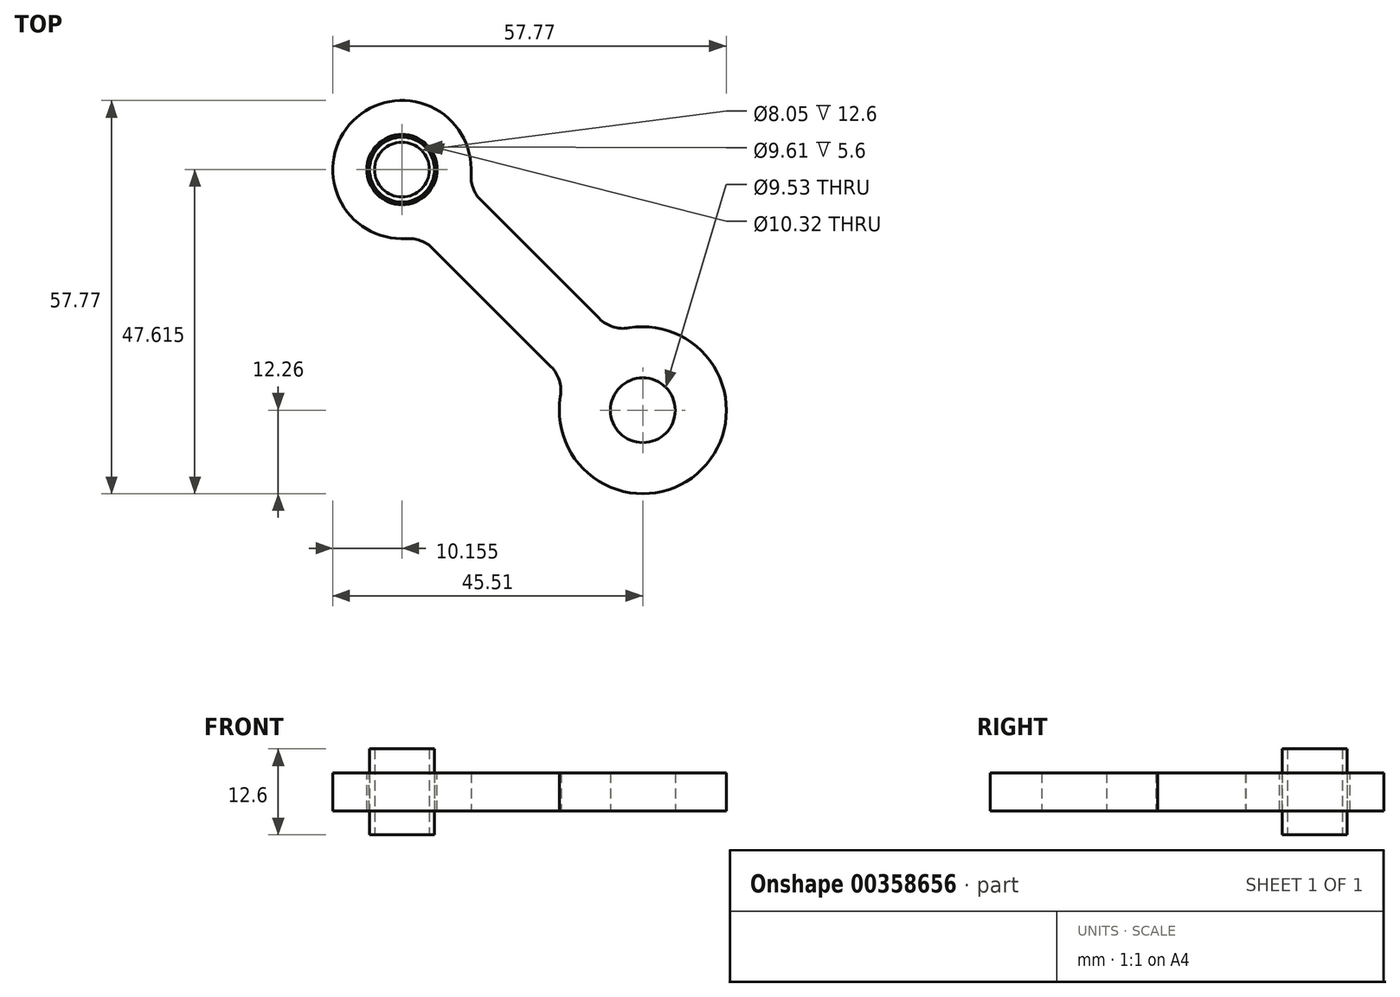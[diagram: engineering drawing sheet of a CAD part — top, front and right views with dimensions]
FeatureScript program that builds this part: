
annotation { "Feature Type Name" : "Feature", "Feature Type Description" : "" }
export const myFeature = defineFeature(function(context is Context, id is Id, definition is map)
    precondition{}
    {
        {
            var Q0;
            Q0=qCreatedBy(makeId("Top.planeOp"),FACE);
            var sketch = newSketch(context, id + "F0", { "sketchPlane" : qUnion([Q0])});
            skCircle(sketch, "E0", {"center": v(0, 0) * mm, "radius": 4.76 * mm});
            skArc(sketch, "E1", {"start": v(10, 7.1) * mm, "mid": v(-12.26, 0) * mm, "end": v(10, -7.1) * mm});
            skCircle(sketch, "E2", {"center": v(50, 0) * mm, "radius": 5.16 * mm});
            skLineSegment(sketch, "E3", {"start": v(0, 0) * mm, "end": v(50, 0) * mm, "construction": true});
            skLineSegment(sketch, "E4", {"start": v(14.07, -5) * mm, "end": v(38.6, -5) * mm});
            skArc(sketch, "E5", {"start": v(14.07, -5) * mm, "mid": v(11.78, -5.56) * mm, "end": v(10, -7.1) * mm});
            skLineSegment(sketch, "E6.trimOffspring", {"start": v(14.07, 5) * mm, "end": v(38.6, 5) * mm});
            skArc(sketch, "E7", {"start": v(10, 7.1) * mm, "mid": v(11.78, 5.56) * mm, "end": v(14.07, 5) * mm});
            skArc(sketch, "E8", {"start": v(42.36, -6.7) * mm, "mid": v(60.16, 0) * mm, "end": v(42.36, 6.7) * mm});
            skArc(sketch, "E9", {"start": v(38.6, 5) * mm, "mid": v(40.67, 5.45) * mm, "end": v(42.36, 6.7) * mm});
            skArc(sketch, "E10", {"start": v(42.36, -6.7) * mm, "mid": v(40.67, -5.45) * mm, "end": v(38.6, -5) * mm});
            skSolve(sketch);
        }
        {
            var Q0;
            Q0=makeQuery(id+"F0.imprint","IMPRINT",FACE,{"disambiguationData":[TD([[makeQuery(id+"F0.imprint","IMPRINT",EDGE,{"derivedFrom":sQuery(id+"F0.wireOp",EDGE,"E0")}),-1.0]])]});
            extrude(context, id + "F1", {"entities" : qUnion([Q0]), "depth" : 5.6 * mm, "offsetDistance" : 25 * mm});
        }
        {
            var Q0;
            Q0=makeQuery(id+"F1.opExtrude","CAP_FACE",FACE,{"disambiguationData":[OSD([sQuery(id+"F0.wireOp",EDGE,"E0"),sQuery(id+"F0.wireOp",EDGE,"E1"),sQuery(id+"F0.wireOp",EDGE,"E2"),sQuery(id+"F0.wireOp",EDGE,"E4"),sQuery(id+"F0.wireOp",EDGE,"E5"),sQuery(id+"F0.wireOp",EDGE,"E6.trimOffspring"),sQuery(id+"F0.wireOp",EDGE,"E7"),sQuery(id+"F0.wireOp",EDGE,"E8"),sQuery(id+"F0.wireOp",EDGE,"E9"),sQuery(id+"F0.wireOp",EDGE,"E10")])],"isStart":false});
            var sketch = newSketch(context, id + "F2", { "sketchPlane" : qUnion([Q0])});
            skCircle(sketch, "E11", {"center": v(50, 0) * mm, "radius": 5.16 * mm});
            skCircle(sketch, "E12", {"center": v(50, 0) * mm, "radius": 4.8 * mm});
            skSolve(sketch);
        }
        {
            var Q0;
            Q0=qSketchRegion(id+"F2",true);
            extrude(context, id + "F3", {"entities" : qUnion([Q0]), "depth" : 0 * mm, "offsetDistance" : 25 * mm, "hasSecondDirection" : true, "secondDirectionOppositeDirection" : true, "secondDirectionDepth" : 5.6 * mm});
        }
        {
            var Q0;
            Q0=makeQuery(id+"F1.opExtrude","CAP_FACE",FACE,{"disambiguationData":[OSD([sQuery(id+"F0.wireOp",EDGE,"E0"),sQuery(id+"F0.wireOp",EDGE,"E1"),sQuery(id+"F0.wireOp",EDGE,"E2"),sQuery(id+"F0.wireOp",EDGE,"E4"),sQuery(id+"F0.wireOp",EDGE,"E5"),sQuery(id+"F0.wireOp",EDGE,"E6.trimOffspring"),sQuery(id+"F0.wireOp",EDGE,"E7"),sQuery(id+"F0.wireOp",EDGE,"E8"),sQuery(id+"F0.wireOp",EDGE,"E9"),sQuery(id+"F0.wireOp",EDGE,"E10")])],"isStart":false});
            var sketch = newSketch(context, id + "F4", { "sketchPlane" : qUnion([Q0])});
            skCircle(sketch, "E13", {"center": v(50, 0) * mm, "radius": 4.76 * mm});
            skCircle(sketch, "E14", {"center": v(50, 0) * mm, "radius": 4.03 * mm});
            skSolve(sketch);
        }
        {
            var Q0;
            Q0=qSketchRegion(id+"F4",true);
            extrude(context, id + "F5", {"entities" : qUnion([Q0]), "depth" : 3.5 * mm, "offsetDistance" : 25 * mm, "hasSecondDirection" : true, "secondDirectionOppositeDirection" : true, "secondDirectionDepth" : (5.6 + 3.5) * mm});
        }
        {
            var Q0;
            Q0=makeQuery(id+"F1.opExtrude","SWEPT_BODY",BODY,{"disambiguationData":[OSD([sQuery(id+"F0.wireOp",EDGE,"E0"),sQuery(id+"F0.wireOp",EDGE,"E1"),sQuery(id+"F0.wireOp",EDGE,"E2"),sQuery(id+"F0.wireOp",EDGE,"E4"),sQuery(id+"F0.wireOp",EDGE,"E5"),sQuery(id+"F0.wireOp",EDGE,"E6.trimOffspring"),sQuery(id+"F0.wireOp",EDGE,"E7"),sQuery(id+"F0.wireOp",EDGE,"E8"),sQuery(id+"F0.wireOp",EDGE,"E9"),sQuery(id+"F0.wireOp",EDGE,"E10")])]});
            var Q1;
            Q1=makeQuery(id+"F5.opExtrude","SWEPT_BODY",BODY,{"disambiguationData":[OSD([sQuery(id+"F4.wireOp",EDGE,"E13"),sQuery(id+"F4.wireOp",EDGE,"E14")])]});
            var Q2;
            Q2=makeQuery(id+"F3.opExtrude","SWEPT_BODY",BODY,{"disambiguationData":[OSD([sQuery(id+"F2.wireOp",EDGE,"E11"),sQuery(id+"F2.wireOp",EDGE,"E12")])]});
            var Q3;
            Q3=makeQuery(id+"F1.opExtrude","CAP_EDGE",EDGE,{"disambiguationData":[OSD([sQuery(id+"F0.wireOp",EDGE,"E0")])],"isStart":false});
            transform(context, id + "F6", {"entities" : qUnion([Q0, Q1, Q2]), "transformType" : TransformType.ROTATION, "transformAxis" : qUnion([Q3]), "angle" : 135 * degree, "makeCopy" : false});
        }
    });
